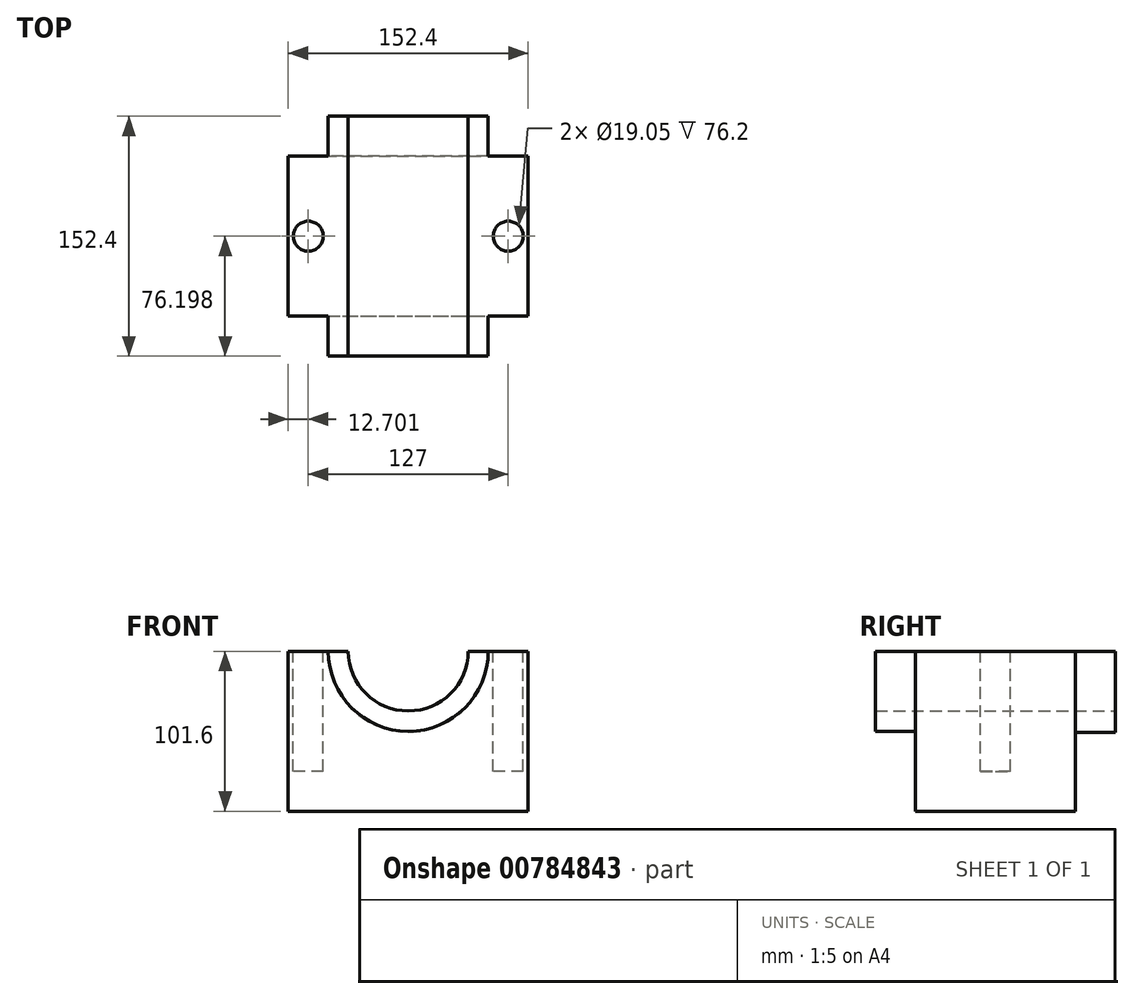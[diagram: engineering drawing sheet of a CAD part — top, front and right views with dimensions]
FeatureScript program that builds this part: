
annotation { "Feature Type Name" : "Feature", "Feature Type Description" : "" }
export const myFeature = defineFeature(function(context is Context, id is Id, definition is map)
    precondition{}
    {
        {
            var Q0;
            Q0=qCreatedBy(makeId("Top.planeOp"),FACE);
            var sketch = newSketch(context, id + "F0", { "sketchPlane" : qUnion([Q0])});
            skLineSegment(sketch, "E0.bottom", {"start": v(-73.84, 75.17) * mm, "end": v(78.56, 75.17) * mm});
            skLineSegment(sketch, "E0.top", {"start": v(-73.84, -26.43) * mm, "end": v(78.56, -26.43) * mm});
            skLineSegment(sketch, "E0.left", {"start": v(-73.84, 75.17) * mm, "end": v(-73.84, -26.43) * mm});
            skLineSegment(sketch, "E0.right", {"start": v(78.56, 75.17) * mm, "end": v(78.56, -26.43) * mm});
            skSolve(sketch);
        }
        {
            var Q0;
            Q0=makeQuery(id+"F0.imprint","IMPRINT",FACE,{"disambiguationData":[TD([[makeQuery(id+"F0.imprint","IMPRINT",EDGE,{"derivedFrom":sQuery(id+"F0.wireOp",EDGE,"E0.bottom")}),-1.0]])]});
            extrude(context, id + "F1", {"entities" : qUnion([Q0]), "depth" : 101.6 * mm, "offsetDistance" : 25.4 * mm});
        }
        {
            var Q0;
            Q0=makeQuery(id+"F1.opExtrude","SWEPT_FACE",FACE,{"disambiguationData":[OSD([sQuery(id+"F0.wireOp",EDGE,"E0.top")])]});
            var sketch = newSketch(context, id + "F2", { "sketchPlane" : qUnion([Q0])});
            skLineSegment(sketch, "E1", {"start": v(-73.84, 101.6) * mm, "end": v(-48.44, 101.6) * mm});
            skLineSegment(sketch, "E2", {"start": v(78.56, 101.6) * mm, "end": v(53.16, 101.6) * mm});
            skArc(sketch, "E3", {"start": v(-48.44, 101.6) * mm, "mid": v(2.36, 50.8) * mm, "end": v(53.16, 101.6) * mm});
            skLineSegment(sketch, "E4", {"start": v(-48.44, 101.6) * mm, "end": v(-35.74, 101.6) * mm});
            skLineSegment(sketch, "E5", {"start": v(53.16, 101.6) * mm, "end": v(40.46, 101.6) * mm});
            skArc(sketch, "E6", {"start": v(-35.74, 101.6) * mm, "mid": v(2.36, 63.72) * mm, "end": v(40.46, 101.6) * mm});
            skSolve(sketch);
        }
        {
            var Q0;
            Q0 = qSketchRegion(id + "F2", true);
            extrude(context, id + "F3", {"entities" : qUnion([Q0]), "operationType" : NewBodyOperationType.ADD, "depth" : 25.4 * mm, "offsetDistance" : 25.4 * mm});
        }
        {
            var Q0;
            {var subQ0=sQuery(id+"F0.wireOp",EDGE,"E0.top");Q0=makeQuery(id+"F3.boolean.opBoolean","SPLIT",FACE,{"disambiguationData":[TD([makeQuery(id+"F3.opExtrude","SWEPT_FACE",FACE,{"disambiguationData":[OSD([sQuery(id+"F2.wireOp",EDGE,"E6")])]})])],"derivedFrom":makeQuery(id+"F1.opExtrude","SWEPT_FACE",FACE,{"disambiguationData":[OSD([subQ0])]})});}
            extrude(context, id + "F4", {"entities" : qUnion([Q0]), "operationType" : NewBodyOperationType.REMOVE, "oppositeDirection" : true, "depth" : 128.27 * mm, "offsetDistance" : 25.4 * mm});
        }
        {
            var Q0;
            Q0=makeQuery(id+"F1.opExtrude","SWEPT_FACE",FACE,{"disambiguationData":[OSD([sQuery(id+"F0.wireOp",EDGE,"E0.bottom")])]});
            var sketch = newSketch(context, id + "F5", { "sketchPlane" : qUnion([Q0])});
            skLineSegment(sketch, "E7", {"start": v(-78.56, 101.6) * mm, "end": v(-53.16, 101.6) * mm});
            skLineSegment(sketch, "E8", {"start": v(73.84, 101.6) * mm, "end": v(48.44, 101.6) * mm});
            skArc(sketch, "E9", {"start": v(-53.16, 101.6) * mm, "mid": v(-2.36, 50.26) * mm, "end": v(48.44, 101.6) * mm});
            skSolve(sketch);
        }
        {
            var Q0;
            {var subQ0=sQuery(id+"F5.wireOp",EDGE,"E9");Q0=makeQuery(id+"F5.imprint","IMPRINT",FACE,{"disambiguationData":[TD([[makeQuery(id+"F5.imprint","IMPRINT",EDGE,{"derivedFrom":subQ0}),1.0]])]});}
            extrude(context, id + "F6", {"entities" : qUnion([Q0]), "operationType" : NewBodyOperationType.ADD, "depth" : 25.4 * mm, "offsetDistance" : 25.4 * mm});
        }
        {
            var Q0;
            {var subQ0=sQuery(id+"F2.wireOp",EDGE,"E4");var subQ1=makeQuery(id+"F3.opExtrude","SWEPT_FACE",FACE,{"disambiguationData":[OSD([subQ0])]});var subQ2=sQuery(id+"F0.wireOp",EDGE,"E0.left");var subQ3=makeQuery(id+"F1.opExtrude","SWEPT_FACE",FACE,{"disambiguationData":[OSD([subQ2])]});var subQ4=sQuery(id+"F0.wireOp",EDGE,"E0.top");var subQ5=sQuery(id+"F0.wireOp",EDGE,"E0.bottom");var subQ6=makeQuery(id+"F1.opExtrude","CAP_FACE",FACE,{"disambiguationData":[OSD([subQ5,subQ4,subQ2,sQuery(id+"F0.wireOp",EDGE,"E0.right")])],"isStart":false});var subQ7=makeQuery(id+"F1.opExtrude","SWEPT_FACE",FACE,{"disambiguationData":[OSD([subQ5])]});var subQ8=sQuery(id+"F2.wireOp",EDGE,"E5");var subQ9=makeQuery(id+"F3.opExtrude","SWEPT_FACE",FACE,{"disambiguationData":[OSD([subQ8])]});var subQ10=sQuery(id+"F2.wireOp",EDGE,"E6");var subQ12=makeQuery(id+"F4.opExtrude","SWEPT_FACE",FACE,{"disambiguationData":[OSD([subQ10])]});var subQ13=makeQuery(id+"F4.boolean.opBoolean","SPLIT",EDGE,{"disambiguationData":[TD([subQ3])],"derivedFrom":makeQuery(id+"F1.opExtrude","CAP_EDGE",EDGE,{"disambiguationData":[OSD([subQ5])],"isStart":false})});Q0=makeQuery(id+"F6.boolean.opBoolean","MERGE",FACE,{"derivedFrom":[makeQuery(id+"F4.boolean.opBoolean","SPLIT",FACE,{"disambiguationData":[TD([subQ3])],"derivedFrom":makeQuery(id+"F3.boolean.opBoolean","MERGE",FACE,{"derivedFrom":[subQ6,subQ1,subQ9]})}),makeQuery(id+"F6.opExtrude","SWEPT_FACE",FACE,{"disambiguationData":[OSD([subQ5]),TDD([makeQuery(id+"F5.imprint","IMPRINT",EDGE,{"disambiguationData":[TD([[makeQuery(id+"F5.imprint","INTERSECT",VERTEX,{"derivedFrom":[makeQuery(id+"F4.boolean.opBoolean","INTERSECT",EDGE,{"derivedFrom":[subQ7,subQ12]}),subQ13]}),1.0]])],"derivedFrom":subQ13})])]})]});}
            var sketch = newSketch(context, id + "F7", { "sketchPlane" : qUnion([Q0])});
            skCircle(sketch, "E10", {"center": v(-61.14, 24.37) * mm, "radius": 9.53 * mm});
            skSolve(sketch);
        }
        {
            var Q0;
            Q0=makeQuery(id+"F7.imprint","IMPRINT",FACE,{"disambiguationData":[TD([[makeQuery(id+"F7.imprint","IMPRINT",EDGE,{"derivedFrom":sQuery(id+"F7.wireOp",EDGE,"E10")}),1.0]])]});
            extrude(context, id + "F8", {"entities" : qUnion([Q0]), "operationType" : NewBodyOperationType.REMOVE, "oppositeDirection" : true, "depth" : 76.2 * mm, "offsetDistance" : 25.4 * mm});
        }
        {
            var Q0;
            {var subQ0=sQuery(id+"F2.wireOp",EDGE,"E4");var subQ1=makeQuery(id+"F3.opExtrude","SWEPT_FACE",FACE,{"disambiguationData":[OSD([subQ0])]});var subQ2=sQuery(id+"F0.wireOp",EDGE,"E0.right");var subQ3=sQuery(id+"F0.wireOp",EDGE,"E0.top");var subQ4=sQuery(id+"F0.wireOp",EDGE,"E0.bottom");var subQ5=makeQuery(id+"F1.opExtrude","CAP_FACE",FACE,{"disambiguationData":[OSD([subQ4,subQ3,sQuery(id+"F0.wireOp",EDGE,"E0.left"),subQ2])],"isStart":false});var subQ6=makeQuery(id+"F1.opExtrude","SWEPT_FACE",FACE,{"disambiguationData":[OSD([subQ2])]});var subQ7=sQuery(id+"F2.wireOp",EDGE,"E5");var subQ8=makeQuery(id+"F3.opExtrude","SWEPT_FACE",FACE,{"disambiguationData":[OSD([subQ7])]});var subQ9=makeQuery(id+"F1.opExtrude","SWEPT_FACE",FACE,{"disambiguationData":[OSD([subQ4])]});var subQ10=sQuery(id+"F2.wireOp",EDGE,"E6");var subQ12=makeQuery(id+"F4.opExtrude","SWEPT_FACE",FACE,{"disambiguationData":[OSD([subQ10])]});var subQ13=makeQuery(id+"F4.boolean.opBoolean","SPLIT",EDGE,{"disambiguationData":[TD([subQ6])],"derivedFrom":makeQuery(id+"F1.opExtrude","CAP_EDGE",EDGE,{"disambiguationData":[OSD([subQ4])],"isStart":false})});Q0=makeQuery(id+"F6.boolean.opBoolean","MERGE",FACE,{"derivedFrom":[makeQuery(id+"F4.boolean.opBoolean","SPLIT",FACE,{"disambiguationData":[TD([subQ6])],"derivedFrom":makeQuery(id+"F3.boolean.opBoolean","MERGE",FACE,{"derivedFrom":[subQ5,subQ1,subQ8]})}),makeQuery(id+"F6.opExtrude","SWEPT_FACE",FACE,{"disambiguationData":[OSD([subQ4]),TDD([makeQuery(id+"F5.imprint","IMPRINT",EDGE,{"disambiguationData":[TD([[makeQuery(id+"F5.imprint","INTERSECT",VERTEX,{"derivedFrom":[makeQuery(id+"F4.boolean.opBoolean","INTERSECT",EDGE,{"derivedFrom":[subQ9,subQ12]}),subQ13]}),-1.0]])],"derivedFrom":subQ13})])]})]});}
            var sketch = newSketch(context, id + "F9", { "sketchPlane" : qUnion([Q0])});
            skCircle(sketch, "E11", {"center": v(65.86, 24.37) * mm, "radius": 9.53 * mm});
            skSolve(sketch);
        }
        {
            var Q0;
            Q0=makeQuery(id+"F9.imprint","IMPRINT",FACE,{"disambiguationData":[TD([[makeQuery(id+"F9.imprint","IMPRINT",EDGE,{"derivedFrom":sQuery(id+"F9.wireOp",EDGE,"E11")}),1.0]])]});
            extrude(context, id + "F10", {"entities" : qUnion([Q0]), "operationType" : NewBodyOperationType.REMOVE, "oppositeDirection" : true, "depth" : 76.2 * mm, "offsetDistance" : 25.4 * mm});
        }
    });
